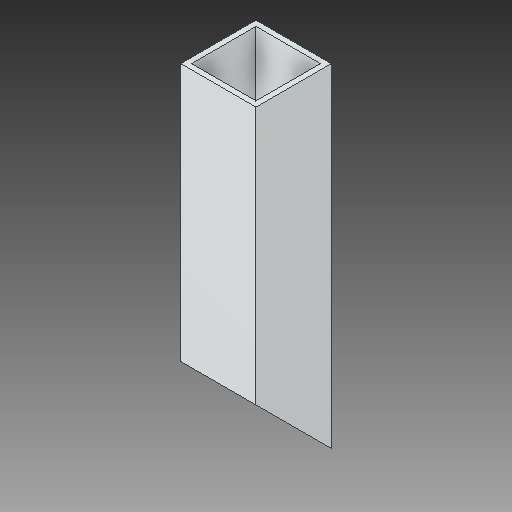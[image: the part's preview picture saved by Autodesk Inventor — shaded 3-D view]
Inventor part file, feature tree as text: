
AUTODESK INVENTOR PART (.ipt)
format: ipt  version: 2018 (Build 220112000, 112)  size: 86,528 bytes
history: native  units: in
note: dims shown in document units (in); Inventor stores cm internally (conversion verified against a paired STEP export)
features: chamfer x1
ambient origin geometry x8: Origin, YZ Plane, XZ Plane, XY Plane, X Axis, Y Axis, Z Axis, Center Point
bodies: Solid1 (feature_tree)
feature tree (1):
  chamfer  "Chamfer1"  [1 undecoded]
note: 1 required parameter value undecoded (feature->parameter linkage not recoverable at this tier; creation-order binding heuristic only, values carry confidence <= 0.55)
